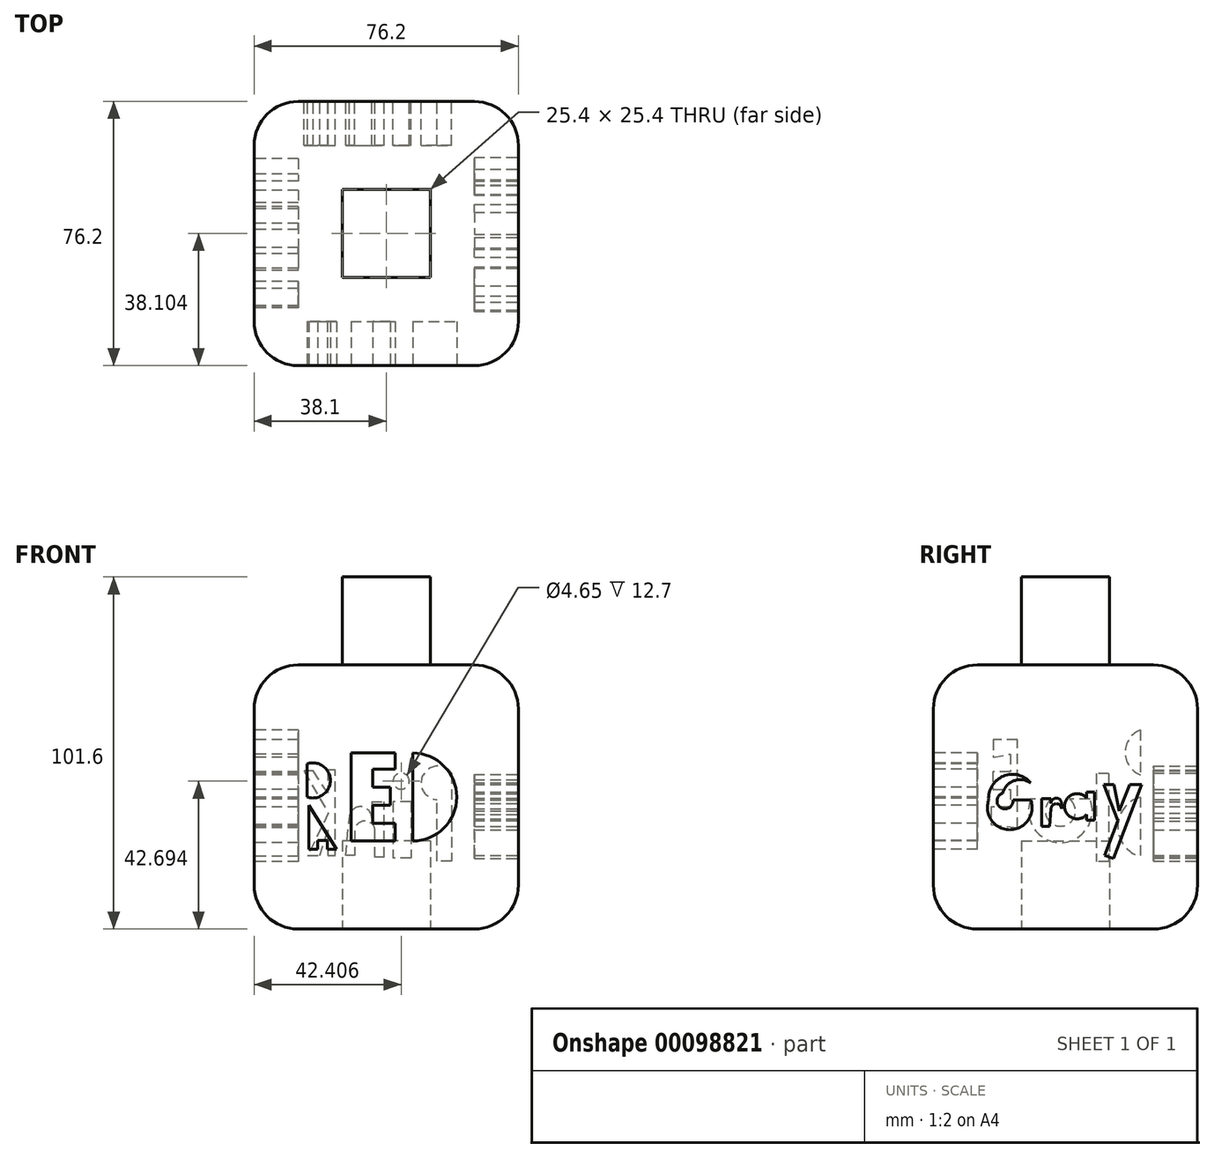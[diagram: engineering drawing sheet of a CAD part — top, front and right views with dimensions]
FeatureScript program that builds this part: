
annotation { "Feature Type Name" : "Feature", "Feature Type Description" : "" }
export const myFeature = defineFeature(function(context is Context, id is Id, definition is map)
    precondition{}
    {
        {
            var Q0;
            Q0=qCreatedBy(makeId("Front.planeOp"),FACE);
            var sketch = newSketch(context, id + "F0", { "sketchPlane" : qUnion([Q0])});
            skLineSegment(sketch, "E0", {"start": v(0, 0) * mm, "end": v(76.2, 0) * mm});
            skLineSegment(sketch, "E1", {"start": v(76.2, 0) * mm, "end": v(76.2, 76.2) * mm});
            skLineSegment(sketch, "E2", {"start": v(76.2, 76.2) * mm, "end": v(0, 76.2) * mm});
            skLineSegment(sketch, "E3", {"start": v(0, 76.2) * mm, "end": v(0, 0) * mm});
            skSolve(sketch);
        }
        {
            var Q0;
            Q0=makeQuery(id+"F0.imprint","IMPRINT",FACE,{"disambiguationData":[TD([[makeQuery(id+"F0.imprint","IMPRINT",EDGE,{"derivedFrom":sQuery(id+"F0.wireOp",EDGE,"E0")}),1.0]])]});
            extrude(context, id + "F1", {"entities" : qUnion([Q0]), "depth" : 76.2 * mm});
        }
        {
            var Q0;
            Q0=makeQuery(id+"F1.opExtrude","CAP_EDGE",EDGE,{"disambiguationData":[OSD([sQuery(id+"F0.wireOp",EDGE,"E2")])],"isStart":false});
            var Q1;
            Q1=makeQuery(id+"F1.opExtrude","SWEPT_EDGE",EDGE,{"disambiguationData":[OSD([sQuery(id+"F0.wireOp",EDGE,"E1"),sQuery(id+"F0.wireOp",EDGE,"E2")])]});
            var Q2;
            Q2=makeQuery(id+"F1.opExtrude","CAP_EDGE",EDGE,{"disambiguationData":[OSD([sQuery(id+"F0.wireOp",EDGE,"E2")])],"isStart":true});
            var Q3;
            Q3=makeQuery(id+"F1.opExtrude","SWEPT_EDGE",EDGE,{"disambiguationData":[OSD([sQuery(id+"F0.wireOp",EDGE,"E2"),sQuery(id+"F0.wireOp",EDGE,"E3")])]});
            var Q4;
            Q4=makeQuery(id+"F1.opExtrude","CAP_EDGE",EDGE,{"disambiguationData":[OSD([sQuery(id+"F0.wireOp",EDGE,"E1")])],"isStart":false});
            var Q5;
            Q5=makeQuery(id+"F1.opExtrude","CAP_EDGE",EDGE,{"disambiguationData":[OSD([sQuery(id+"F0.wireOp",EDGE,"E1")])],"isStart":true});
            var Q6;
            Q6=makeQuery(id+"F1.opExtrude","CAP_EDGE",EDGE,{"disambiguationData":[OSD([sQuery(id+"F0.wireOp",EDGE,"E3")])],"isStart":false});
            var Q7;
            Q7=makeQuery(id+"F1.opExtrude","CAP_EDGE",EDGE,{"disambiguationData":[OSD([sQuery(id+"F0.wireOp",EDGE,"E3")])],"isStart":true});
            var Q8;
            Q8=makeQuery(id+"F1.opExtrude","SWEPT_EDGE",EDGE,{"disambiguationData":[OSD([sQuery(id+"F0.wireOp",EDGE,"E0"),sQuery(id+"F0.wireOp",EDGE,"E3")])]});
            var Q9;
            Q9=makeQuery(id+"F1.opExtrude","CAP_EDGE",EDGE,{"disambiguationData":[OSD([sQuery(id+"F0.wireOp",EDGE,"E0")])],"isStart":true});
            var Q10;
            Q10=makeQuery(id+"F1.opExtrude","SWEPT_EDGE",EDGE,{"disambiguationData":[OSD([sQuery(id+"F0.wireOp",EDGE,"E0"),sQuery(id+"F0.wireOp",EDGE,"E1")])]});
            var Q11;
            Q11=makeQuery(id+"F1.opExtrude","CAP_EDGE",EDGE,{"disambiguationData":[OSD([sQuery(id+"F0.wireOp",EDGE,"E0")])],"isStart":false});
            fillet(context, id + "F2", {"entities" : qUnion([Q0, Q1, Q2, Q3, Q4, Q5, Q6, Q7, Q8, Q9, Q10, Q11]), "radius" : 12.7 * mm, "tangentPropagation" : true, "allowEdgeOverflow" : false});
        }
        {
            var Q0;
            Q0=makeQuery(id+"F1.opExtrude","CAP_FACE",FACE,{"disambiguationData":[OSD([sQuery(id+"F0.wireOp",EDGE,"E0"),sQuery(id+"F0.wireOp",EDGE,"E1"),sQuery(id+"F0.wireOp",EDGE,"E2"),sQuery(id+"F0.wireOp",EDGE,"E3")])],"isStart":false});
            var sketch = newSketch(context, id + "F3", { "sketchPlane" : qUnion([Q0])});
            skLineSegment(sketch, "E4", {"start": v(15.24, 38.1) * mm, "end": v(15.24, 25.4) * mm});
            skLineSegment(sketch, "E5", {"start": v(15.24, 25.4) * mm, "end": v(22.86, 25.4) * mm});
            skLineSegment(sketch, "E6", {"start": v(22.86, 25.4) * mm, "end": v(15.24, 38.1) * mm});
            skLineSegment(sketch, "E7", {"start": v(27.94, 25.4) * mm, "end": v(27.94, 50.8) * mm});
            skLineSegment(sketch, "E8", {"start": v(27.94, 50.8) * mm, "end": v(40.64, 50.8) * mm});
            skLineSegment(sketch, "E9", {"start": v(40.64, 50.8) * mm, "end": v(40.64, 46.17) * mm});
            skLineSegment(sketch, "E10", {"start": v(40.64, 46.17) * mm, "end": v(34.15, 46.17) * mm});
            skLineSegment(sketch, "E11", {"start": v(34.15, 46.17) * mm, "end": v(34.15, 40.97) * mm});
            skLineSegment(sketch, "E12", {"start": v(34.15, 40.97) * mm, "end": v(39.34, 40.97) * mm});
            skLineSegment(sketch, "E13", {"start": v(39.34, 40.97) * mm, "end": v(39.34, 35.78) * mm});
            skLineSegment(sketch, "E14", {"start": v(39.34, 35.78) * mm, "end": v(34.15, 35.78) * mm});
            skLineSegment(sketch, "E15", {"start": v(34.15, 35.78) * mm, "end": v(34.15, 30.6) * mm});
            skLineSegment(sketch, "E16", {"start": v(34.15, 30.6) * mm, "end": v(40.64, 30.6) * mm});
            skLineSegment(sketch, "E17", {"start": v(27.94, 25.4) * mm, "end": v(40.64, 25.4) * mm});
            skLineSegment(sketch, "E18", {"start": v(40.64, 25.4) * mm, "end": v(40.64, 30.6) * mm});
            skLineSegment(sketch, "E19", {"start": v(45.72, 50.8) * mm, "end": v(45.72, 25.4) * mm});
            skArc(sketch, "E20", {"start": v(45.72, 25.4) * mm, "mid": v(58.42, 38.1) * mm, "end": v(45.72, 50.8) * mm});
            skLineSegment(sketch, "E21", {"start": v(15.24, 38.1) * mm, "end": v(15.24, 47.7) * mm});
            skArc(sketch, "E22", {"start": v(15.24, 38.1) * mm, "mid": v(22, 42.9) * mm, "end": v(15.24, 47.7) * mm});
            skSolve(sketch);
        }
        {
            var Q0;
            Q0=makeQuery(id+"F3.imprint","IMPRINT",FACE,{"disambiguationData":[TD([[makeQuery(id+"F3.imprint","IMPRINT",EDGE,{"derivedFrom":sQuery(id+"F3.wireOp",EDGE,"E21")}),-1.0]])]});
            var Q1;
            Q1=makeQuery(id+"F3.imprint","IMPRINT",FACE,{"disambiguationData":[TD([[makeQuery(id+"F3.imprint","IMPRINT",EDGE,{"derivedFrom":sQuery(id+"F3.wireOp",EDGE,"E7")}),-1.0]])]});
            var Q2;
            Q2=makeQuery(id+"F3.imprint","IMPRINT",FACE,{"disambiguationData":[TD([[makeQuery(id+"F3.imprint","IMPRINT",EDGE,{"derivedFrom":sQuery(id+"F3.wireOp",EDGE,"E19")}),1.0]])]});
            extrude(context, id + "F4", {"entities" : qUnion([Q0, Q1, Q2]), "operationType" : NewBodyOperationType.REMOVE, "oppositeDirection" : true, "depth" : 12.7 * mm});
        }
        {
            var Q0;
            Q0=makeQuery(id+"F1.opExtrude","CAP_FACE",FACE,{"disambiguationData":[OSD([sQuery(id+"F0.wireOp",EDGE,"E0"),sQuery(id+"F0.wireOp",EDGE,"E1"),sQuery(id+"F0.wireOp",EDGE,"E2"),sQuery(id+"F0.wireOp",EDGE,"E3")])],"isStart":false});
            var sketch = newSketch(context, id + "F5", { "sketchPlane" : qUnion([Q0])});
            skLineSegment(sketch, "E23", {"start": v(15.85, 35.67) * mm, "end": v(15.85, 22.97) * mm});
            skLineSegment(sketch, "E24", {"start": v(15.85, 22.97) * mm, "end": v(18.4, 22.97) * mm});
            skLineSegment(sketch, "E25", {"start": v(18.4, 22.97) * mm, "end": v(18.4, 25.51) * mm});
            skLineSegment(sketch, "E26", {"start": v(18.4, 25.51) * mm, "end": v(21.19, 25.51) * mm});
            skLineSegment(sketch, "E27", {"start": v(21.19, 25.51) * mm, "end": v(21.19, 22.97) * mm});
            skLineSegment(sketch, "E28", {"start": v(21.19, 22.97) * mm, "end": v(23.73, 22.97) * mm});
            skLineSegment(sketch, "E29", {"start": v(23.73, 22.97) * mm, "end": v(15.85, 35.67) * mm});
            skSolve(sketch);
        }
        {
            var Q0;
            Q0=makeQuery(id+"F5.imprint","IMPRINT",FACE,{"disambiguationData":[TD([[makeQuery(id+"F5.imprint","IMPRINT",EDGE,{"derivedFrom":sQuery(id+"F5.wireOp",EDGE,"E23")}),1.0]])]});
            extrude(context, id + "F6", {"entities" : qUnion([Q0]), "operationType" : NewBodyOperationType.REMOVE, "oppositeDirection" : true, "depth" : 12.7 * mm});
        }
        {
            var Q0;
            Q0=makeQuery(id+"F1.opExtrude","SWEPT_FACE",FACE,{"disambiguationData":[OSD([sQuery(id+"F0.wireOp",EDGE,"E0")])]});
            var sketch = newSketch(context, id + "F7", { "sketchPlane" : qUnion([Q0])});
            skLineSegment(sketch, "E30", {"start": v(25.4, 50.8) * mm, "end": v(25.4, 25.4) * mm});
            skLineSegment(sketch, "E31", {"start": v(25.4, 25.4) * mm, "end": v(50.8, 25.4) * mm});
            skLineSegment(sketch, "E32", {"start": v(50.8, 25.4) * mm, "end": v(50.8, 50.8) * mm});
            skLineSegment(sketch, "E33", {"start": v(50.8, 50.8) * mm, "end": v(25.4, 50.8) * mm});
            skSolve(sketch);
        }
        {
            var Q0;
            Q0=makeQuery(id+"F7.imprint","IMPRINT",FACE,{"disambiguationData":[TD([[makeQuery(id+"F7.imprint","IMPRINT",EDGE,{"derivedFrom":sQuery(id+"F7.wireOp",EDGE,"E30")}),1.0]])]});
            extrude(context, id + "F8", {"entities" : qUnion([Q0]), "operationType" : NewBodyOperationType.REMOVE, "oppositeDirection" : true, "depth" : 25.4 * mm});
        }
        {
            var Q0;
            Q0=makeQuery(id+"F1.opExtrude","SWEPT_FACE",FACE,{"disambiguationData":[OSD([sQuery(id+"F0.wireOp",EDGE,"E2")])]});
            var sketch = newSketch(context, id + "F9", { "sketchPlane" : qUnion([Q0])});
            skLineSegment(sketch, "E34", {"start": v(25.4, -25.4) * mm, "end": v(25.4, -50.8) * mm});
            skLineSegment(sketch, "E35", {"start": v(25.4, -50.8) * mm, "end": v(50.8, -50.8) * mm});
            skLineSegment(sketch, "E36", {"start": v(50.8, -50.8) * mm, "end": v(50.8, -25.4) * mm});
            skLineSegment(sketch, "E37", {"start": v(50.8, -25.4) * mm, "end": v(25.4, -25.4) * mm});
            skSolve(sketch);
        }
        {
            var Q0;
            Q0=makeQuery(id+"F9.imprint","IMPRINT",FACE,{"disambiguationData":[TD([[makeQuery(id+"F9.imprint","IMPRINT",EDGE,{"derivedFrom":sQuery(id+"F9.wireOp",EDGE,"E34")}),1.0]])]});
            extrude(context, id + "F10", {"entities" : qUnion([Q0]), "operationType" : NewBodyOperationType.ADD, "depth" : 25.4 * mm});
        }
        {
            var Q0;
            Q0=makeQuery(id+"F1.opExtrude","SWEPT_FACE",FACE,{"disambiguationData":[OSD([sQuery(id+"F0.wireOp",EDGE,"E3")])]});
            var sketch = newSketch(context, id + "F11", { "sketchPlane" : qUnion([Q0])});
            skLineSegment(sketch, "E38", {"start": v(16.55, 57.43) * mm, "end": v(16.55, 44.5) * mm});
            skLineSegment(sketch, "E39", {"start": v(16.55, 38.04) * mm, "end": v(16.55, 20.97) * mm});
            skArc(sketch, "E40", {"start": v(16.55, 44.5) * mm, "mid": v(20.9, 50.97) * mm, "end": v(16.55, 57.43) * mm});
            skArc(sketch, "E41", {"start": v(16.55, 20.97) * mm, "mid": v(23.01, 29.5) * mm, "end": v(16.55, 38.04) * mm});
            skLineSegment(sketch, "E42.bottom", {"start": v(25.6, 44.82) * mm, "end": v(29.22, 44.82) * mm});
            skLineSegment(sketch, "E42.top", {"start": v(25.6, 19.42) * mm, "end": v(29.22, 19.42) * mm});
            skLineSegment(sketch, "E42.left", {"start": v(25.6, 44.82) * mm, "end": v(25.6, 19.42) * mm});
            skLineSegment(sketch, "E42.right", {"start": v(29.22, 44.82) * mm, "end": v(29.22, 19.42) * mm});
            skLineSegment(sketch, "E43", {"start": v(31.03, 37.52) * mm, "end": v(36.98, 37.52) * mm});
            skLineSegment(sketch, "E44", {"start": v(42.15, 37.52) * mm, "end": v(48.1, 37.52) * mm});
            skArc(sketch, "E45", {"start": v(31.03, 37.52) * mm, "mid": v(39.56, 24.96) * mm, "end": v(48.1, 37.52) * mm});
            skArc(sketch, "E46", {"start": v(36.98, 37.52) * mm, "mid": v(39.56, 29.7) * mm, "end": v(42.15, 37.52) * mm});
            skLineSegment(sketch, "E47", {"start": v(51.97, 29.24) * mm, "end": v(51.97, 54.64) * mm});
            skLineSegment(sketch, "E48", {"start": v(51.97, 54.64) * mm, "end": v(58.98, 54.64) * mm});
            skLineSegment(sketch, "E49", {"start": v(58.98, 54.64) * mm, "end": v(58.98, 49.56) * mm});
            skLineSegment(sketch, "E50", {"start": v(58.98, 49.56) * mm, "end": v(53.99, 50.5) * mm});
            skLineSegment(sketch, "E51", {"start": v(53.99, 50.5) * mm, "end": v(53.99, 45.42) * mm});
            skLineSegment(sketch, "E52", {"start": v(53.99, 45.42) * mm, "end": v(59.07, 45.42) * mm});
            skLineSegment(sketch, "E53", {"start": v(59.07, 45.42) * mm, "end": v(59.07, 40.34) * mm});
            skLineSegment(sketch, "E54", {"start": v(59.07, 40.34) * mm, "end": v(53.99, 40.34) * mm});
            skLineSegment(sketch, "E55", {"start": v(53.99, 40.34) * mm, "end": v(53.99, 35.26) * mm});
            skLineSegment(sketch, "E56", {"start": v(53.99, 35.26) * mm, "end": v(59.53, 35.26) * mm});
            skLineSegment(sketch, "E57", {"start": v(59.53, 35.26) * mm, "end": v(59.53, 30.18) * mm});
            skLineSegment(sketch, "E58", {"start": v(59.53, 30.18) * mm, "end": v(51.97, 29.24) * mm});
            skSolve(sketch);
        }
        {
            var Q0;
            Q0=makeQuery(id+"F11.imprint","IMPRINT",FACE,{"disambiguationData":[TD([[makeQuery(id+"F11.imprint","IMPRINT",EDGE,{"derivedFrom":sQuery(id+"F11.wireOp",EDGE,"E38")}),1.0]])]});
            var Q1;
            Q1=makeQuery(id+"F11.imprint","IMPRINT",FACE,{"disambiguationData":[TD([[makeQuery(id+"F11.imprint","IMPRINT",EDGE,{"derivedFrom":sQuery(id+"F11.wireOp",EDGE,"E39")}),1.0]])]});
            var Q2;
            Q2=makeQuery(id+"F11.imprint","IMPRINT",FACE,{"disambiguationData":[TD([[makeQuery(id+"F11.imprint","IMPRINT",EDGE,{"derivedFrom":sQuery(id+"F11.wireOp",EDGE,"E42.bottom")}),-1.0]])]});
            var Q3;
            Q3=makeQuery(id+"F11.imprint","IMPRINT",FACE,{"disambiguationData":[TD([[makeQuery(id+"F11.imprint","IMPRINT",EDGE,{"derivedFrom":sQuery(id+"F11.wireOp",EDGE,"E43")}),-1.0]])]});
            var Q4;
            Q4=makeQuery(id+"F11.imprint","IMPRINT",FACE,{"disambiguationData":[TD([[makeQuery(id+"F11.imprint","IMPRINT",EDGE,{"derivedFrom":sQuery(id+"F11.wireOp",EDGE,"E47")}),-1.0]])]});
            extrude(context, id + "F12", {"entities" : qUnion([Q0, Q1, Q2, Q3, Q4]), "operationType" : NewBodyOperationType.REMOVE, "oppositeDirection" : true, "depth" : 12.7 * mm});
        }
        {
            var Q0;
            Q0=makeQuery(id+"F1.opExtrude","CAP_FACE",FACE,{"disambiguationData":[OSD([sQuery(id+"F0.wireOp",EDGE,"E0"),sQuery(id+"F0.wireOp",EDGE,"E1"),sQuery(id+"F0.wireOp",EDGE,"E2"),sQuery(id+"F0.wireOp",EDGE,"E3")])],"isStart":true});
            var sketch = newSketch(context, id + "F13", { "sketchPlane" : qUnion([Q0])});
            skLineSegment(sketch, "E59", {"start": v(-56.96, 44.96) * mm, "end": v(-56.96, 19.56) * mm});
            skLineSegment(sketch, "E60", {"start": v(-56.96, 19.56) * mm, "end": v(-52.72, 19.56) * mm});
            skLineSegment(sketch, "E61", {"start": v(-52.72, 19.56) * mm, "end": v(-52.72, 37.38) * mm});
            skArc(sketch, "E62", {"start": v(-52.72, 37.38) * mm, "mid": v(-48.8, 44.55) * mm, "end": v(-56.96, 44.96) * mm});
            skLineSegment(sketch, "E63.bottom", {"start": v(-45.25, 36.75) * mm, "end": v(-40.08, 36.75) * mm});
            skLineSegment(sketch, "E63.top", {"start": v(-45.25, 20.46) * mm, "end": v(-40.08, 20.46) * mm});
            skLineSegment(sketch, "E63.left", {"start": v(-45.25, 36.75) * mm, "end": v(-45.25, 20.46) * mm});
            skLineSegment(sketch, "E63.right", {"start": v(-40.08, 36.75) * mm, "end": v(-40.08, 20.46) * mm});
            skCircle(sketch, "E64", {"center": v(-42.4, 42.7) * mm, "radius": 2.33 * mm});
            skLineSegment(sketch, "E65", {"start": v(-37.5, 20.72) * mm, "end": v(-34.9, 20.72) * mm});
            skLineSegment(sketch, "E66", {"start": v(-37.5, 20.72) * mm, "end": v(-37.5, 36.75) * mm});
            skLineSegment(sketch, "E67", {"start": v(-33.92, 36.75) * mm, "end": v(-37.5, 36.75) * mm});
            skLineSegment(sketch, "E68", {"start": v(-33.92, 36.75) * mm, "end": v(-33.92, 32.1) * mm});
            skArc(sketch, "E69", {"start": v(-27.45, 32.1) * mm, "mid": v(-30.69, 35.33) * mm, "end": v(-33.92, 32.1) * mm});
            skLineSegment(sketch, "E70", {"start": v(-34.9, 20.72) * mm, "end": v(-34.9, 28.21) * mm});
            skArc(sketch, "E71", {"start": v(-28.96, 28.21) * mm, "mid": v(-31.93, 31.19) * mm, "end": v(-34.9, 28.21) * mm});
            skLineSegment(sketch, "E72", {"start": v(-28.96, 28.21) * mm, "end": v(-28.96, 21.23) * mm});
            skLineSegment(sketch, "E73", {"start": v(-28.96, 21.23) * mm, "end": v(-26.42, 21.23) * mm});
            skLineSegment(sketch, "E74", {"start": v(-26.42, 21.23) * mm, "end": v(-27.45, 32.1) * mm});
            skLineSegment(sketch, "E75", {"start": v(-23.46, 21.23) * mm, "end": v(-23.46, 45.89) * mm});
            skLineSegment(sketch, "E76", {"start": v(-23.46, 45.89) * mm, "end": v(-21.3, 45.89) * mm});
            skLineSegment(sketch, "E77", {"start": v(-21.3, 45.89) * mm, "end": v(-21.3, 39.24) * mm});
            skLineSegment(sketch, "E78", {"start": v(-21.3, 39.24) * mm, "end": v(-17.09, 45.61) * mm});
            skLineSegment(sketch, "E79", {"start": v(-17.09, 45.61) * mm, "end": v(-14.38, 45.61) * mm});
            skLineSegment(sketch, "E80", {"start": v(-14.38, 45.61) * mm, "end": v(-21.43, 33.4) * mm});
            skLineSegment(sketch, "E81", {"start": v(-21.43, 33.4) * mm, "end": v(-15.46, 21.2) * mm});
            skLineSegment(sketch, "E82", {"start": v(-15.46, 21.2) * mm, "end": v(-18.99, 21.2) * mm});
            skLineSegment(sketch, "E83", {"start": v(-18.99, 21.2) * mm, "end": v(-21.3, 28.66) * mm});
            skLineSegment(sketch, "E84", {"start": v(-21.3, 28.66) * mm, "end": v(-21.3, 21.2) * mm});
            skLineSegment(sketch, "E85", {"start": v(-21.3, 21.2) * mm, "end": v(-23.46, 21.23) * mm});
            skSolve(sketch);
        }
        {
            var Q0;
            Q0=makeQuery(id+"F13.imprint","IMPRINT",FACE,{"disambiguationData":[TD([[makeQuery(id+"F13.imprint","IMPRINT",EDGE,{"derivedFrom":sQuery(id+"F13.wireOp",EDGE,"E59")}),1.0]])]});
            var Q1;
            Q1=makeQuery(id+"F13.imprint","IMPRINT",FACE,{"disambiguationData":[TD([[makeQuery(id+"F13.imprint","IMPRINT",EDGE,{"derivedFrom":sQuery(id+"F13.wireOp",EDGE,"E63.bottom")}),-1.0]])]});
            var Q2;
            Q2=makeQuery(id+"F13.imprint","IMPRINT",FACE,{"disambiguationData":[TD([[makeQuery(id+"F13.imprint","IMPRINT",EDGE,{"derivedFrom":sQuery(id+"F13.wireOp",EDGE,"E65")}),1.0]])]});
            var Q3;
            Q3=makeQuery(id+"F13.imprint","IMPRINT",FACE,{"disambiguationData":[TD([[makeQuery(id+"F13.imprint","IMPRINT",EDGE,{"derivedFrom":sQuery(id+"F13.wireOp",EDGE,"E75")}),-1.0]])]});
            var Q4;
            Q4=makeQuery(id+"F13.imprint","IMPRINT",FACE,{"disambiguationData":[TD([[makeQuery(id+"F13.imprint","IMPRINT",EDGE,{"derivedFrom":sQuery(id+"F13.wireOp",EDGE,"E64")}),1.0]])]});
            extrude(context, id + "F14", {"entities" : qUnion([Q0, Q1, Q2, Q3, Q4]), "operationType" : NewBodyOperationType.REMOVE, "oppositeDirection" : true, "depth" : 12.7 * mm});
        }
        {
            var Q0;
            Q0=makeQuery(id+"F1.opExtrude","SWEPT_FACE",FACE,{"disambiguationData":[OSD([sQuery(id+"F0.wireOp",EDGE,"E1")])]});
            var sketch = newSketch(context, id + "F15", { "sketchPlane" : qUnion([Q0])});
            skLineSegment(sketch, "E86", {"start": v(-53.27, 37.26) * mm, "end": v(-48.1, 37.26) * mm});
            skArc(sketch, "E87", {"start": v(-60.25, 37.26) * mm, "mid": v(-54.17, 28.67) * mm, "end": v(-48.1, 37.26) * mm});
            skArc(sketch, "E88", {"start": v(-48.1, 42.18) * mm, "mid": v(-55.96, 44.16) * mm, "end": v(-60.25, 37.26) * mm});
            skArc(sketch, "E89", {"start": v(-48.1, 42.18) * mm, "mid": v(-52.92, 42.8) * mm, "end": v(-56.18, 39.18) * mm});
            skArc(sketch, "E90", {"start": v(-56.18, 39.18) * mm, "mid": v(-56.81, 35.04) * mm, "end": v(-53.27, 37.26) * mm});
            skLineSegment(sketch, "E91", {"start": v(-45, 29.66) * mm, "end": v(-42.61, 29.66) * mm});
            skLineSegment(sketch, "E92", {"start": v(-45, 29.66) * mm, "end": v(-45, 37.64) * mm});
            skLineSegment(sketch, "E93", {"start": v(-45, 37.64) * mm, "end": v(-42.24, 37.64) * mm});
            skLineSegment(sketch, "E94", {"start": v(-42.24, 37.64) * mm, "end": v(-42.24, 36.3) * mm});
            skArc(sketch, "E95", {"start": v(-39.25, 36.3) * mm, "mid": v(-40.74, 37.8) * mm, "end": v(-42.24, 36.3) * mm});
            skLineSegment(sketch, "E96", {"start": v(-39.25, 36.3) * mm, "end": v(-39.25, 34.69) * mm});
            skArc(sketch, "E97", {"start": v(-39.25, 34.69) * mm, "mid": v(-40.74, 36.18) * mm, "end": v(-42.24, 34.69) * mm});
            skLineSegment(sketch, "E98", {"start": v(-42.24, 34.69) * mm, "end": v(-42.61, 29.66) * mm});
            skCircle(sketch, "E99", {"center": v(-34.75, 35.43) * mm, "radius": 3.64 * mm});
            skLineSegment(sketch, "E100.bottom", {"start": v(-31.97, 39.5) * mm, "end": v(-29.72, 39.5) * mm});
            skLineSegment(sketch, "E100.top", {"start": v(-31.97, 31.47) * mm, "end": v(-29.72, 31.47) * mm});
            skLineSegment(sketch, "E100.left", {"start": v(-31.97, 39.5) * mm, "end": v(-31.97, 31.47) * mm});
            skLineSegment(sketch, "E100.right", {"start": v(-29.72, 39.5) * mm, "end": v(-29.72, 31.47) * mm});
            skLineSegment(sketch, "E101", {"start": v(-27.04, 41.75) * mm, "end": v(-24.15, 41.75) * mm});
            skLineSegment(sketch, "E102", {"start": v(-24.15, 41.75) * mm, "end": v(-22.65, 34.04) * mm});
            skLineSegment(sketch, "E103", {"start": v(-22.65, 34.04) * mm, "end": v(-19.55, 41.75) * mm});
            skLineSegment(sketch, "E104", {"start": v(-19.55, 41.75) * mm, "end": v(-16.12, 41.75) * mm});
            skLineSegment(sketch, "E105", {"start": v(-16.12, 41.75) * mm, "end": v(-24.26, 20.34) * mm});
            skLineSegment(sketch, "E106", {"start": v(-24.26, 20.34) * mm, "end": v(-26.79, 21.3) * mm});
            skLineSegment(sketch, "E107", {"start": v(-26.79, 21.3) * mm, "end": v(-23, 31.27) * mm});
            skLineSegment(sketch, "E108", {"start": v(-23, 31.27) * mm, "end": v(-27.04, 41.75) * mm});
            skSolve(sketch);
        }
        {
            var Q0;
            Q0 = qSketchRegion(id + "F15", true);
            extrude(context, id + "F16", {"entities" : qUnion([Q0]), "operationType" : NewBodyOperationType.REMOVE, "oppositeDirection" : true, "depth" : 12.7 * mm});
        }
    });
